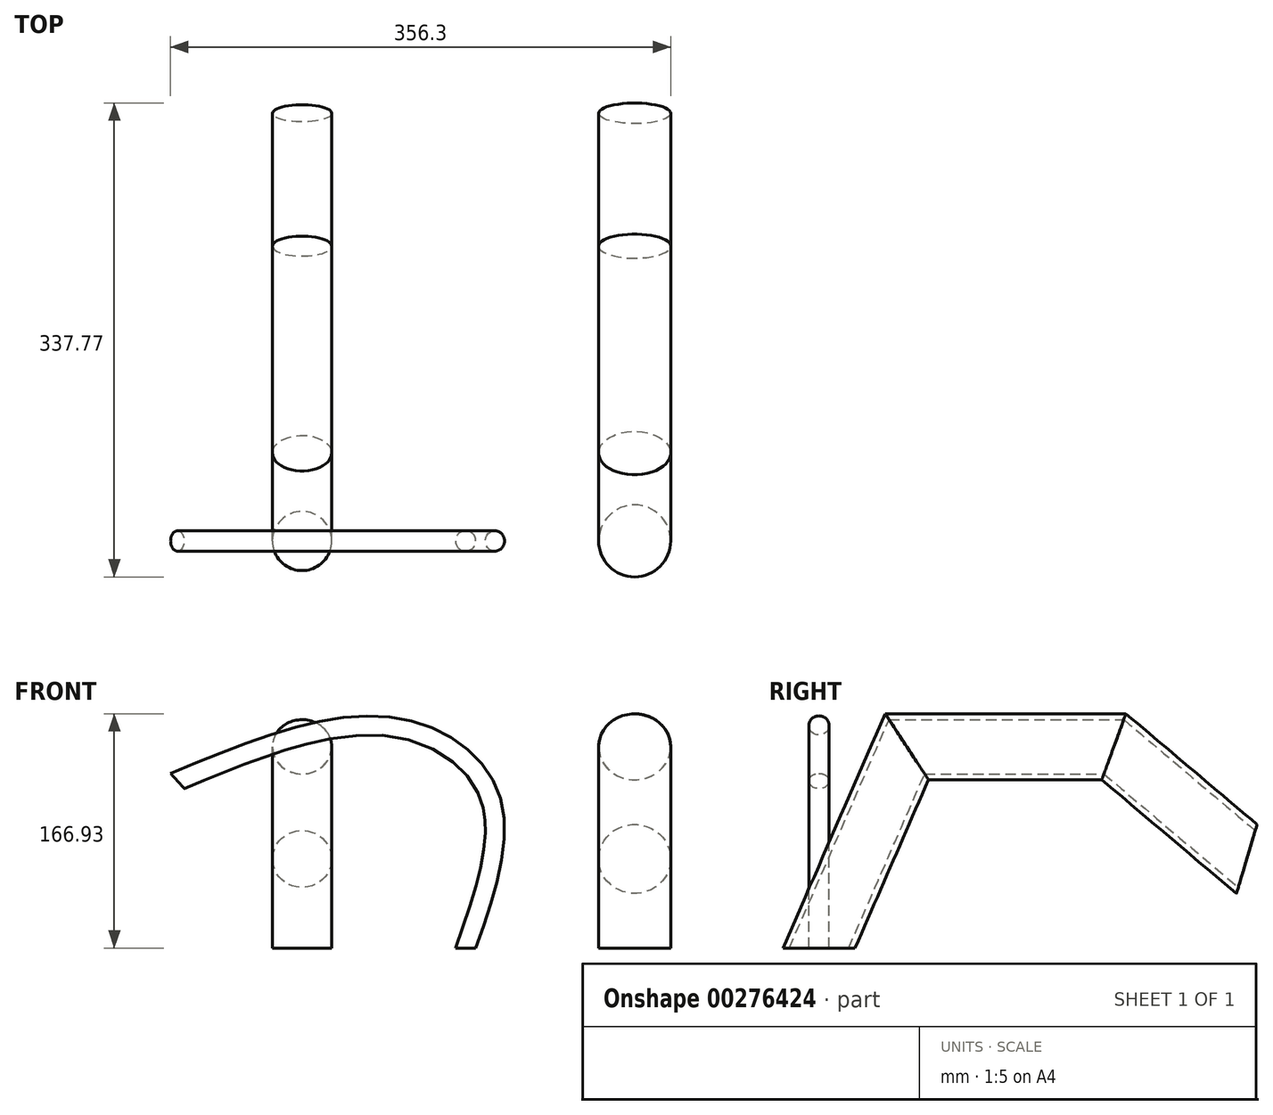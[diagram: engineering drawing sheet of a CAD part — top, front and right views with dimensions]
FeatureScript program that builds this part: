
annotation { "Feature Type Name" : "Feature", "Feature Type Description" : "" }
export const myFeature = defineFeature(function(context is Context, id is Id, definition is map)
    precondition{}
    {
        {
            var Q0;
            Q0=qCreatedBy(makeId("Top.planeOp"),FACE);
            var sketch = newSketch(context, id + "F0", { "sketchPlane" : qUnion([Q0])});
            skCircle(sketch, "E0", {"center": v(0, 0) * mm, "radius": 25.74 * mm});
            skCircle(sketch, "E1", {"center": v(-116.54, 0) * mm, "radius": 21.12 * mm});
            skCircle(sketch, "E2", {"center": v(120.39, 0) * mm, "radius": 25.67 * mm});
            skCircle(sketch, "E3.cCircle", {"center": v(0, 0) * mm, "radius": 52.74 * mm, "construction": true});
            skLineSegment(sketch, "E3.0", {"start": v(20.7, 48.51) * mm, "end": v(52.36, 6.32) * mm});
            skLineSegment(sketch, "E3.1", {"start": v(52.36, 6.32) * mm, "end": v(31.66, -42.19) * mm});
            skLineSegment(sketch, "E3.2", {"start": v(31.66, -42.19) * mm, "end": v(-20.7, -48.51) * mm});
            skLineSegment(sketch, "E3.3", {"start": v(-20.7, -48.51) * mm, "end": v(-52.36, -6.32) * mm});
            skLineSegment(sketch, "E3.4", {"start": v(-52.36, -6.32) * mm, "end": v(-31.66, 42.19) * mm});
            skLineSegment(sketch, "E3.5", {"start": v(-31.66, 42.19) * mm, "end": v(20.7, 48.51) * mm});
            skCircle(sketch, "E4", {"center": v(0, 0) * mm, "radius": 7.24 * mm});
            skSolve(sketch);
        }
        {
            var Q0;
            Q0=qCreatedBy(makeId("Front.planeOp"),FACE);
            var sketch = newSketch(context, id + "F1", { "sketchPlane" : qUnion([Q0])});
            skFitSpline(sketch, "E5", {"points": [v(0, 0) * mm, v(17.13, 108.07) * mm, v(-54.23, 157.82) * mm, v(-205.4, 119.04) * mm], "startDerivative": vector(127.77, 362.18) * mm, "endDerivative": vector(-412.6, -170.87) * mm});
            skSolve(sketch);
        }
        {
            var Q0;
            Q0=makeQuery(id+"F0.imprint","IMPRINT",FACE,{"disambiguationData":[TD([[makeQuery(id+"F0.imprint","IMPRINT",EDGE,{"derivedFrom":sQuery(id+"F0.wireOp",EDGE,"E4")}),1.0]])]});
            var Q1;
            Q1=sQuery(id+"F1.wireOp",EDGE,"E5");
            sweep(context, id + "F2", {"profiles" : qUnion([Q0]), "path" : qUnion([Q1])});
        }
        {
            var Q0;
            Q0=qCreatedBy(makeId("Right.planeOp"),FACE);
            var sketch = newSketch(context, id + "F3", { "sketchPlane" : qUnion([Q0])});
            skLineSegment(sketch, "E6", {"start": v(0, 0) * mm, "end": v(62.61, 143.4) * mm});
            skLineSegment(sketch, "E7", {"start": v(62.61, 143.4) * mm, "end": v(210.1, 143.4) * mm});
            skLineSegment(sketch, "E8", {"start": v(210.1, 143.4) * mm, "end": v(304.77, 63.46) * mm});
            skSolve(sketch);
        }
        {
            var Q0;
            Q0=makeQuery(id+"F0.imprint","IMPRINT",FACE,{"disambiguationData":[TD([[makeQuery(id+"F0.imprint","IMPRINT",EDGE,{"derivedFrom":sQuery(id+"F0.wireOp",EDGE,"E2")}),1.0]])]});
            var Q1;
            Q1=makeQuery(id+"F0.imprint","IMPRINT",FACE,{"disambiguationData":[TD([[makeQuery(id+"F0.imprint","IMPRINT",EDGE,{"derivedFrom":sQuery(id+"F0.wireOp",EDGE,"E1")}),1.0]])]});
            var Q2;
            Q2=sQuery(id+"F3.wireOp",EDGE,"E6");
            var Q3;
            Q3=sQuery(id+"F3.wireOp",EDGE,"E7");
            var Q4;
            Q4=sQuery(id+"F3.wireOp",EDGE,"E8");
            sweep(context, id + "F4", {"profiles" : qUnion([Q0, Q1]), "path" : qUnion([Q2, Q3, Q4])});
        }
    });
